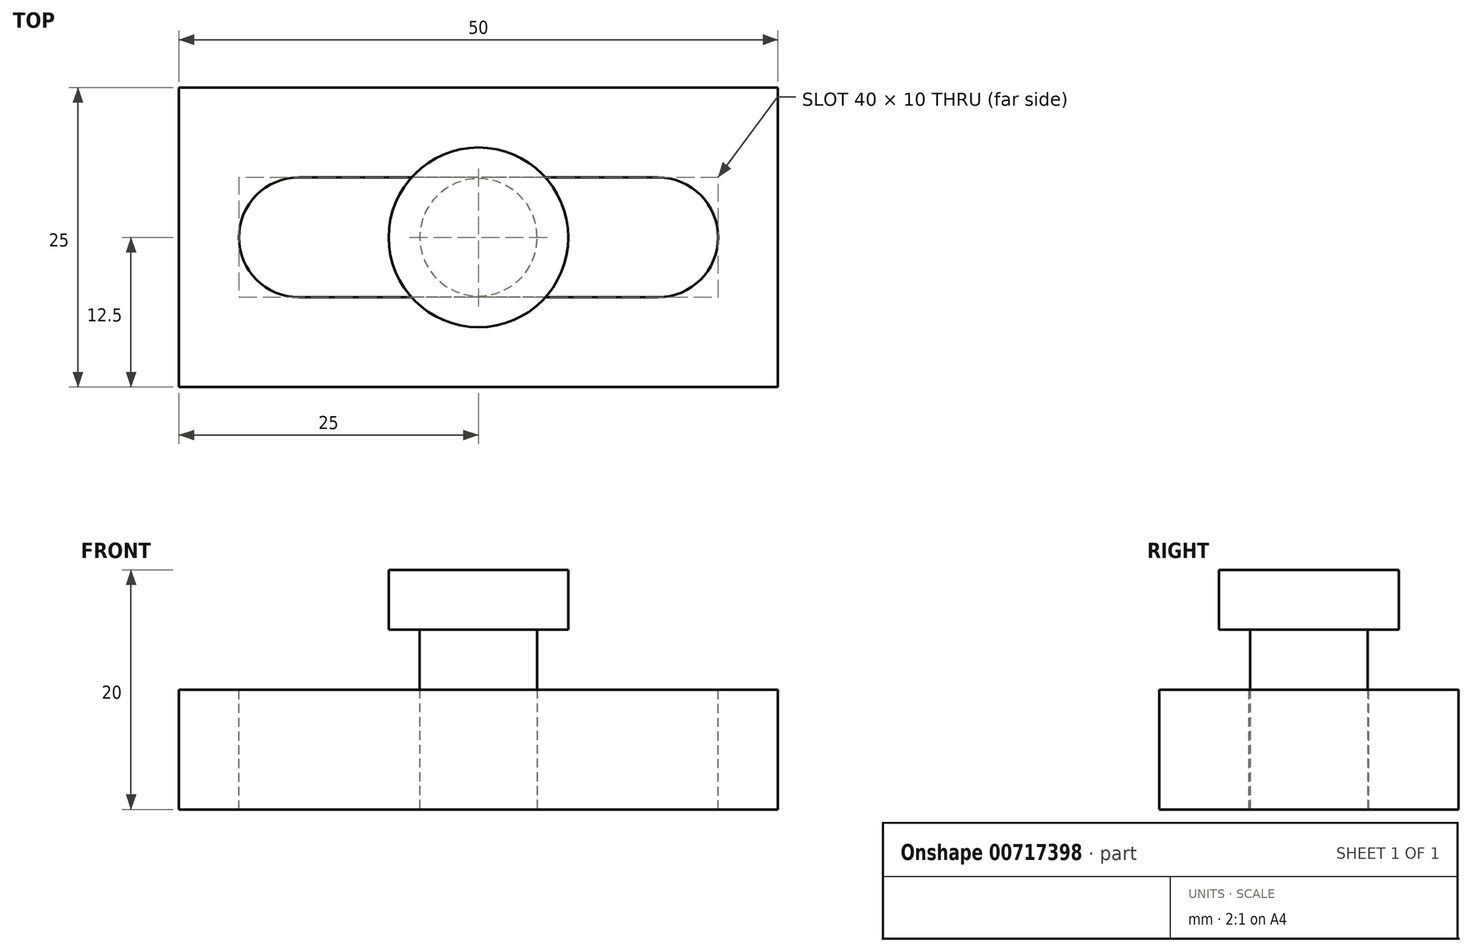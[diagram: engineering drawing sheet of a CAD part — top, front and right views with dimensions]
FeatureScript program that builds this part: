
annotation { "Feature Type Name" : "Feature", "Feature Type Description" : "" }
export const myFeature = defineFeature(function(context is Context, id is Id, definition is map)
    precondition{}
    {
        {
            var Q0;
            Q0=qCreatedBy(makeId("Top.planeOp"),FACE);
            var sketch = newSketch(context, id + "F0", { "sketchPlane" : qUnion([Q0])});
            skLineSegment(sketch, "E0.bottom", {"start": v(25, 12.5) * mm, "end": v(-25, 12.5) * mm});
            skLineSegment(sketch, "E0.top", {"start": v(25, -12.5) * mm, "end": v(-25, -12.5) * mm});
            skLineSegment(sketch, "E0.left", {"start": v(25, 12.5) * mm, "end": v(25, -12.5) * mm});
            skLineSegment(sketch, "E0.right", {"start": v(-25, 12.5) * mm, "end": v(-25, -12.5) * mm});
            skPoint(sketch, "E0.middle", {"position": v(0, 0) * mm});
            skSolve(sketch);
        }
        {
            var Q0;
            Q0=makeQuery(id+"F0.imprint","IMPRINT",FACE,{"disambiguationData":[TD([[makeQuery(id+"F0.imprint","IMPRINT",EDGE,{"derivedFrom":sQuery(id+"F0.wireOp",EDGE,"E0.bottom")}),1.0]])]});
            extrude(context, id + "F1", {"entities" : qUnion([Q0]), "depth" : 10 * mm, "offsetDistance" : 25 * mm});
        }
        {
            var Q0;
            Q0=makeQuery(id+"F1.opExtrude","CAP_FACE",FACE,{"disambiguationData":[OSD([sQuery(id+"F0.wireOp",EDGE,"E0.bottom"),sQuery(id+"F0.wireOp",EDGE,"E0.top"),sQuery(id+"F0.wireOp",EDGE,"E0.left"),sQuery(id+"F0.wireOp",EDGE,"E0.right")])],"isStart":false});
            var sketch = newSketch(context, id + "F2", { "sketchPlane" : qUnion([Q0])});
            skLineSegment(sketch, "E1.bottom", {"start": v(15, 5) * mm, "end": v(-15, 5) * mm});
            skLineSegment(sketch, "E1.top", {"start": v(15, -5) * mm, "end": v(-15, -5) * mm});
            skLineSegment(sketch, "E1.left", {"start": v(15, 5) * mm, "end": v(15, -5) * mm, "construction": true});
            skLineSegment(sketch, "E1.right", {"start": v(-15, 5) * mm, "end": v(-15, -5) * mm, "construction": true});
            skPoint(sketch, "E1.middle", {"position": v(0, 0) * mm});
            skArc(sketch, "E2", {"start": v(-15, 5) * mm, "mid": v(-20, 0) * mm, "end": v(-15, -5) * mm});
            skArc(sketch, "E3", {"start": v(15, -5) * mm, "mid": v(20, 0) * mm, "end": v(15, 5) * mm});
            skSolve(sketch);
        }
        {
            var Q0;
            Q0=makeQuery(id+"F2.imprint","IMPRINT",FACE,{"disambiguationData":[TD([[makeQuery(id+"F2.imprint","IMPRINT",EDGE,{"derivedFrom":sQuery(id+"F2.wireOp",EDGE,"E1.bottom")}),1.0]])]});
            extrude(context, id + "F3", {"entities" : qUnion([Q0]), "operationType" : NewBodyOperationType.REMOVE, "endBound" : BoundingType.THROUGH_ALL, "oppositeDirection" : true, "depth" : 25 * mm, "offsetDistance" : 25 * mm});
        }
        {
            var Q0;
            Q0=makeQuery(id+"F1.opExtrude","CAP_FACE",FACE,{"disambiguationData":[OSD([sQuery(id+"F0.wireOp",EDGE,"E0.bottom"),sQuery(id+"F0.wireOp",EDGE,"E0.top"),sQuery(id+"F0.wireOp",EDGE,"E0.left"),sQuery(id+"F0.wireOp",EDGE,"E0.right")])],"isStart":false});
            var sketch = newSketch(context, id + "F4", { "sketchPlane" : qUnion([Q0])});
            skCircle(sketch, "E4", {"center": v(0, 0) * mm, "radius": 4.9 * mm});
            skSolve(sketch);
        }
        {
            var Q0;
            Q0=makeQuery(id+"F4.imprint","IMPRINT",FACE,{"disambiguationData":[TD([[makeQuery(id+"F4.imprint","IMPRINT",EDGE,{"derivedFrom":sQuery(id+"F4.wireOp",EDGE,"E4")}),1.0]])]});
            extrude(context, id + "F5", {"entities" : qUnion([Q0]), "depth" : 5 * mm, "offsetDistance" : 25 * mm, "hasSecondDirection" : true, "secondDirectionOppositeDirection" : true, "secondDirectionDepth" : 10 * mm});
        }
        {
            var Q0;
            Q0=makeQuery(id+"F5.opExtrude","CAP_FACE",FACE,{"disambiguationData":[OSD([sQuery(id+"F4.wireOp",EDGE,"E4")])],"isStart":false});
            var sketch = newSketch(context, id + "F6", { "sketchPlane" : qUnion([Q0])});
            skCircle(sketch, "E5", {"center": v(0, 0) * mm, "radius": 7.5 * mm});
            skSolve(sketch);
        }
        {
            var Q0;
            Q0=makeQuery(id+"F6.imprint","IMPRINT",FACE,{"disambiguationData":[TD([[makeQuery(id+"F6.imprint","IMPRINT",EDGE,{"derivedFrom":sQuery(id+"F6.wireOp",EDGE,"E5")}),1.0]])]});
            var Q1;
            Q1=makeQuery(id+"F6.imprint","IMPRINT",FACE,{"disambiguationData":[TD([[makeQuery(id+"F6.imprint","IMPRINT",EDGE,{"derivedFrom":makeQuery(id+"F5.opExtrude","CAP_EDGE",EDGE,{"disambiguationData":[OSD([sQuery(id+"F4.wireOp",EDGE,"E4")])],"isStart":false})}),1.0]])]});
            extrude(context, id + "F7", {"entities" : qUnion([Q0, Q1]), "operationType" : NewBodyOperationType.ADD, "depth" : 5 * mm, "offsetDistance" : 25 * mm});
        }
    });
